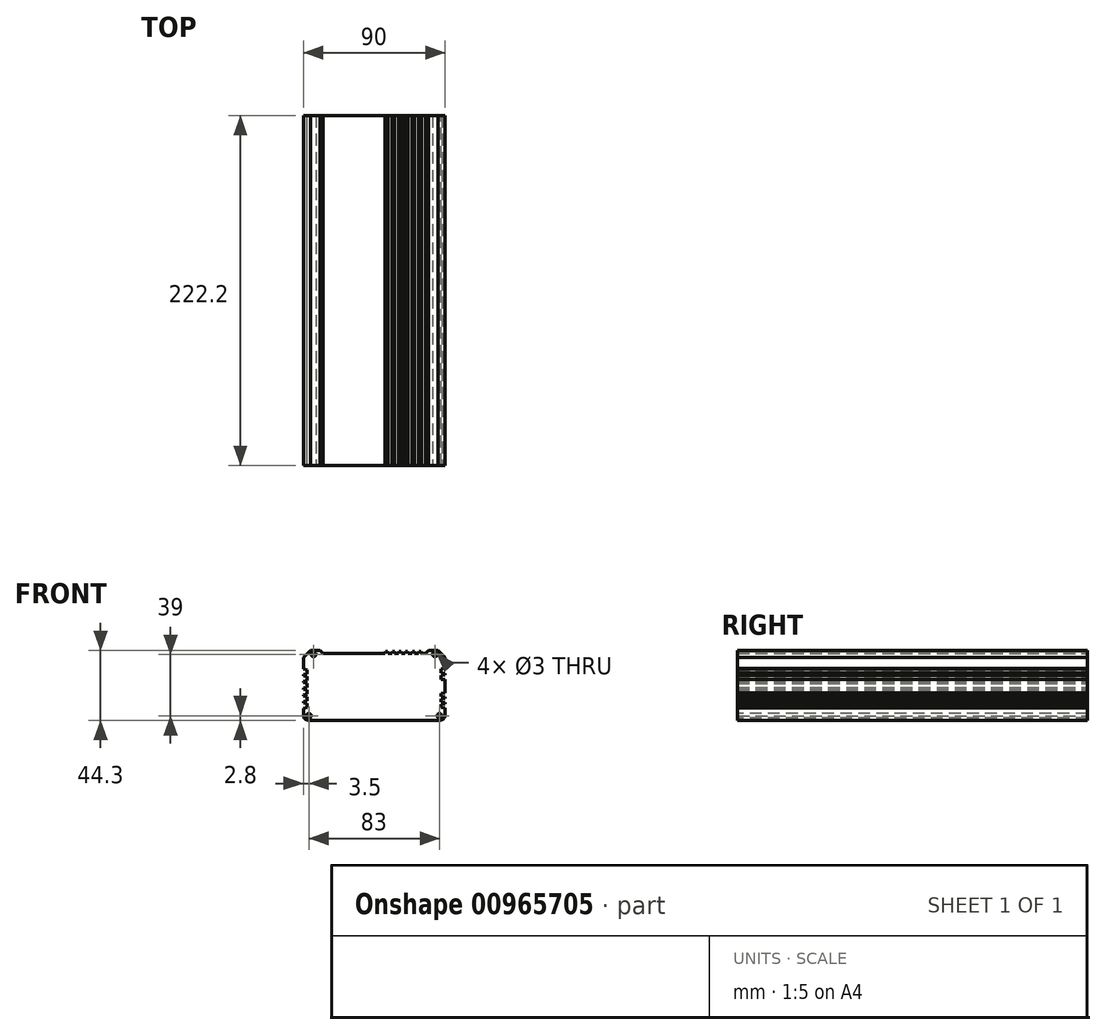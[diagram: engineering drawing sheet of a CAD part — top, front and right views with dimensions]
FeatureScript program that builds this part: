
annotation { "Feature Type Name" : "Feature", "Feature Type Description" : "" }
export const myFeature = defineFeature(function(context is Context, id is Id, definition is map)
    precondition{}
    {
        {
            var Q0;
            Q0=qCreatedBy(makeId("Front.planeOp"),FACE);
            var sketch = newSketch(context, id + "F0", { "sketchPlane" : qUnion([Q0])});
            skLineSegment(sketch, "E0", {"start": v(28.5, 43.8) * mm, "end": v(28.25, 42.3) * mm});
            skLineSegment(sketch, "E1", {"start": v(28.25, 42.3) * mm, "end": v(25.75, 42.3) * mm});
            skLineSegment(sketch, "E2", {"start": v(25.75, 42.3) * mm, "end": v(25.5, 43.8) * mm});
            skPoint(sketch, "E3", {"position": v(27, 42.3) * mm});
            skPoint(sketch, "E4", {"position": v(27, 43.3) * mm});
            skPoint(sketch, "E5.1.0.1", {"position": v(22.75, 42.3) * mm});
            skLineSegment(sketch, "E5.1.0.3", {"start": v(24.25, 43.8) * mm, "end": v(24, 42.3) * mm});
            skLineSegment(sketch, "E5.1.0.4", {"start": v(24, 42.3) * mm, "end": v(21.5, 42.3) * mm});
            skLineSegment(sketch, "E5.1.0.5", {"start": v(21.5, 42.3) * mm, "end": v(21.25, 43.8) * mm});
            skPoint(sketch, "E5.2.0.1", {"position": v(18.5, 42.3) * mm});
            skLineSegment(sketch, "E5.2.0.3", {"start": v(20, 43.8) * mm, "end": v(19.75, 42.3) * mm});
            skLineSegment(sketch, "E5.2.0.4", {"start": v(19.75, 42.3) * mm, "end": v(17.25, 42.3) * mm});
            skLineSegment(sketch, "E5.2.0.5", {"start": v(17.25, 42.3) * mm, "end": v(17, 43.8) * mm});
            skPoint(sketch, "E5.3.0.1", {"position": v(14.25, 42.3) * mm});
            skLineSegment(sketch, "E5.3.0.3", {"start": v(15.75, 43.8) * mm, "end": v(15.5, 42.3) * mm});
            skLineSegment(sketch, "E5.3.0.4", {"start": v(15.5, 42.3) * mm, "end": v(13, 42.3) * mm});
            skLineSegment(sketch, "E5.3.0.5", {"start": v(13, 42.3) * mm, "end": v(12.75, 43.8) * mm});
            skPoint(sketch, "E5.4.0.1", {"position": v(10, 42.3) * mm});
            skLineSegment(sketch, "E5.4.0.3", {"start": v(11.5, 43.8) * mm, "end": v(11.25, 42.3) * mm});
            skLineSegment(sketch, "E5.4.0.4", {"start": v(11.25, 42.3) * mm, "end": v(8.75, 42.3) * mm});
            skLineSegment(sketch, "E5.4.0.5", {"start": v(8.75, 42.3) * mm, "end": v(8.5, 43.8) * mm});
            skLineSegment(sketch, "E5.direction1", {"start": v(25.75, 42.3) * mm, "end": v(21.5, 42.3) * mm, "construction": true});
            skLineSegment(sketch, "E6", {"start": v(34.5, 44.3) * mm, "end": v(32.5, 42.3) * mm});
            skLineSegment(sketch, "E7", {"start": v(32.5, 42.3) * mm, "end": v(30, 42.3) * mm});
            skLineSegment(sketch, "E8", {"start": v(30, 42.3) * mm, "end": v(29.75, 43.8) * mm});
            skLineSegment(sketch, "E9", {"start": v(24.25, 43.8) * mm, "end": v(25.5, 43.8) * mm});
            skLineSegment(sketch, "E10", {"start": v(28.5, 43.8) * mm, "end": v(29.75, 43.8) * mm});
            skLineSegment(sketch, "E11", {"start": v(19.75, 42.3) * mm, "end": v(21.5, 42.3) * mm, "construction": true});
            skLineSegment(sketch, "E12", {"start": v(28.25, 42.3) * mm, "end": v(30, 42.3) * mm, "construction": true});
            skLineSegment(sketch, "E13", {"start": v(45, 39.8) * mm, "end": v(40.5, 44.3) * mm});
            skLineSegment(sketch, "E14.MirrorCS", {"start": v(-45, 39.8) * mm, "end": v(-40.5, 44.3) * mm});
            skLineSegment(sketch, "E15.MirrorCS", {"start": v(-34.5, 44.3) * mm, "end": v(-32.5, 42.3) * mm});
            skLineSegment(sketch, "E16", {"start": v(-32.5, 42.3) * mm, "end": v(7, 42.3) * mm});
            skLineSegment(sketch, "E17", {"start": v(7, 42.3) * mm, "end": v(7.25, 43.8) * mm});
            skLineSegment(sketch, "E18", {"start": v(8.75, 42.3) * mm, "end": v(7, 42.3) * mm, "construction": true});
            skLineSegment(sketch, "E19", {"start": v(8.5, 43.8) * mm, "end": v(7.25, 43.8) * mm});
            skLineSegment(sketch, "E20", {"start": v(42.5, 17) * mm, "end": v(42.5, 15) * mm});
            skLineSegment(sketch, "E21", {"start": v(42.5, 15) * mm, "end": v(45, 14.75) * mm});
            skLineSegment(sketch, "E22", {"start": v(45, 17.25) * mm, "end": v(42.5, 17) * mm});
            skPoint(sketch, "E23", {"position": v(42.5, 16) * mm});
            skPoint(sketch, "E24.1.0.0", {"position": v(42.5, 12.5) * mm});
            skLineSegment(sketch, "E24.1.0.2", {"start": v(45, 13.75) * mm, "end": v(42.5, 13.5) * mm});
            skLineSegment(sketch, "E24.1.0.3", {"start": v(42.5, 11.5) * mm, "end": v(45, 11.25) * mm});
            skLineSegment(sketch, "E24.1.0.5", {"start": v(42.5, 13.5) * mm, "end": v(42.5, 11.5) * mm});
            skPoint(sketch, "E24.2.0.0", {"position": v(42.5, 9) * mm});
            skLineSegment(sketch, "E24.2.0.2", {"start": v(45, 10.25) * mm, "end": v(42.5, 10) * mm});
            skLineSegment(sketch, "E24.2.0.3", {"start": v(42.5, 8) * mm, "end": v(45, 7.75) * mm});
            skLineSegment(sketch, "E24.2.0.5", {"start": v(42.5, 10) * mm, "end": v(42.5, 8) * mm});
            skLineSegment(sketch, "E24.direction1", {"start": v(42.5, 15) * mm, "end": v(42.5, 11.5) * mm, "construction": true});
            skLineSegment(sketch, "E25", {"start": v(45, 32.75) * mm, "end": v(42.5, 32.5) * mm});
            skLineSegment(sketch, "E26", {"start": v(42.5, 32.5) * mm, "end": v(42.5, 30) * mm});
            skLineSegment(sketch, "E27", {"start": v(42.5, 30) * mm, "end": v(45, 29.75) * mm});
            skPoint(sketch, "E28", {"position": v(42.5, 31.25) * mm});
            skPoint(sketch, "E29.1.0.0", {"position": v(42.5, 27.25) * mm});
            skLineSegment(sketch, "E29.1.0.1", {"start": v(45, 28.75) * mm, "end": v(42.5, 28.5) * mm});
            skLineSegment(sketch, "E29.1.0.2", {"start": v(42.5, 28.5) * mm, "end": v(42.5, 26) * mm});
            skLineSegment(sketch, "E29.1.0.4", {"start": v(42.5, 26) * mm, "end": v(45, 25.75) * mm});
            skLineSegment(sketch, "E29.direction1", {"start": v(42.5, 30) * mm, "end": v(42.5, 26) * mm, "construction": true});
            skLineSegment(sketch, "E30.MirrorCS", {"start": v(-42.5, 29.5) * mm, "end": v(-45, 29) * mm});
            skLineSegment(sketch, "E31.MirrorCS", {"start": v(-45, 32.5) * mm, "end": v(-42.5, 32) * mm});
            skLineSegment(sketch, "E32.MirrorCS", {"start": v(-42.5, 32) * mm, "end": v(-42.5, 29.5) * mm});
            skLineSegment(sketch, "E33", {"start": v(-45, 39.8) * mm, "end": v(-45, 32.5) * mm});
            skLineSegment(sketch, "E34", {"start": v(40.5, 44.3) * mm, "end": v(34.5, 44.3) * mm});
            skLineSegment(sketch, "E35", {"start": v(11.5, 43.8) * mm, "end": v(12.75, 43.8) * mm});
            skLineSegment(sketch, "E36", {"start": v(15.75, 43.8) * mm, "end": v(17, 43.8) * mm});
            skLineSegment(sketch, "E37", {"start": v(20, 43.8) * mm, "end": v(21.25, 43.8) * mm});
            skLineSegment(sketch, "E38", {"start": v(45, 39.8) * mm, "end": v(45, 32.75) * mm});
            skLineSegment(sketch, "E39", {"start": v(45, 29.75) * mm, "end": v(45, 28.75) * mm});
            skLineSegment(sketch, "E40", {"start": v(45, 25.75) * mm, "end": v(45, 17.25) * mm});
            skLineSegment(sketch, "E41", {"start": v(45, 14.75) * mm, "end": v(45, 13.75) * mm});
            skLineSegment(sketch, "E42", {"start": v(45, 11.25) * mm, "end": v(45, 10.25) * mm});
            skLineSegment(sketch, "E43", {"start": v(-45, 29) * mm, "end": v(-45, 28.2) * mm});
            skLineSegment(sketch, "E44", {"start": v(-42.01, 0) * mm, "end": v(42, 0) * mm});
            skLineSegment(sketch, "E45", {"start": v(45, 3) * mm, "end": v(45, 7.75) * mm});
            skArc(sketch, "E46.filletArc", {"start": v(-45, 2.75) * mm, "mid": v(-44.04, 0.8) * mm, "end": v(-42.01, 0) * mm});
            skArc(sketch, "E47.filletArc", {"start": v(42, 0) * mm, "mid": v(44.12, 0.88) * mm, "end": v(45, 3) * mm});
            skLineSegment(sketch, "E48", {"start": v(-40.5, 44.3) * mm, "end": v(-34.5, 44.3) * mm});
            skPoint(sketch, "E49.positionSnap0", {"position": v(-42.5, 30.75) * mm});
            skLineSegment(sketch, "E50", {"start": v(-45, 32.5) * mm, "end": v(-45, 29) * mm, "construction": true});
            skPoint(sketch, "E51", {"position": v(-45, 30.75) * mm});
            skPoint(sketch, "E52.1.0.0", {"position": v(-45, 26.45) * mm});
            skLineSegment(sketch, "E52.1.0.1", {"start": v(-45, 28.2) * mm, "end": v(-42.5, 27.7) * mm});
            skLineSegment(sketch, "E52.1.0.2", {"start": v(-42.5, 25.2) * mm, "end": v(-45, 24.7) * mm});
            skPoint(sketch, "E52.1.0.3", {"position": v(-42.5, 26.45) * mm});
            skLineSegment(sketch, "E52.1.0.4", {"start": v(-42.5, 27.7) * mm, "end": v(-42.5, 25.2) * mm});
            skLineSegment(sketch, "E52.1.0.5", {"start": v(-45, 24.7) * mm, "end": v(-45, 23.9) * mm});
            skLineSegment(sketch, "E52.1.0.6", {"start": v(-45, 28.2) * mm, "end": v(-45, 24.7) * mm, "construction": true});
            skPoint(sketch, "E52.2.0.0", {"position": v(-45, 22.15) * mm});
            skLineSegment(sketch, "E52.2.0.1", {"start": v(-45, 23.9) * mm, "end": v(-42.5, 23.4) * mm});
            skLineSegment(sketch, "E52.2.0.2", {"start": v(-42.5, 20.9) * mm, "end": v(-45, 20.4) * mm});
            skPoint(sketch, "E52.2.0.3", {"position": v(-42.5, 22.15) * mm});
            skLineSegment(sketch, "E52.2.0.4", {"start": v(-42.5, 23.4) * mm, "end": v(-42.5, 20.9) * mm});
            skLineSegment(sketch, "E52.2.0.5", {"start": v(-45, 20.4) * mm, "end": v(-45, 19.6) * mm});
            skLineSegment(sketch, "E52.2.0.6", {"start": v(-45, 23.9) * mm, "end": v(-45, 20.4) * mm, "construction": true});
            skPoint(sketch, "E52.3.0.0", {"position": v(-45, 17.85) * mm});
            skLineSegment(sketch, "E52.3.0.1", {"start": v(-45, 19.6) * mm, "end": v(-42.5, 19.1) * mm});
            skLineSegment(sketch, "E52.3.0.2", {"start": v(-42.5, 16.6) * mm, "end": v(-45, 16.1) * mm});
            skPoint(sketch, "E52.3.0.3", {"position": v(-42.5, 17.85) * mm});
            skLineSegment(sketch, "E52.3.0.4", {"start": v(-42.5, 19.1) * mm, "end": v(-42.5, 16.6) * mm});
            skLineSegment(sketch, "E52.3.0.5", {"start": v(-45, 16.1) * mm, "end": v(-45, 15.3) * mm});
            skLineSegment(sketch, "E52.3.0.6", {"start": v(-45, 19.6) * mm, "end": v(-45, 16.1) * mm, "construction": true});
            skPoint(sketch, "E52.4.0.0", {"position": v(-45, 13.55) * mm});
            skLineSegment(sketch, "E52.4.0.1", {"start": v(-45, 15.3) * mm, "end": v(-42.5, 14.8) * mm});
            skLineSegment(sketch, "E52.4.0.2", {"start": v(-42.5, 12.3) * mm, "end": v(-45, 11.8) * mm});
            skPoint(sketch, "E52.4.0.3", {"position": v(-42.5, 13.55) * mm});
            skLineSegment(sketch, "E52.4.0.4", {"start": v(-42.5, 14.8) * mm, "end": v(-42.5, 12.3) * mm});
            skLineSegment(sketch, "E52.4.0.5", {"start": v(-45, 11.8) * mm, "end": v(-45, 11) * mm});
            skLineSegment(sketch, "E52.4.0.6", {"start": v(-45, 15.3) * mm, "end": v(-45, 11.8) * mm, "construction": true});
            skPoint(sketch, "E52.5.0.0", {"position": v(-45, 9.25) * mm});
            skLineSegment(sketch, "E52.5.0.1", {"start": v(-45, 11) * mm, "end": v(-42.5, 10.5) * mm});
            skLineSegment(sketch, "E52.5.0.2", {"start": v(-42.5, 8) * mm, "end": v(-45, 7.5) * mm});
            skPoint(sketch, "E52.5.0.3", {"position": v(-42.5, 9.25) * mm});
            skLineSegment(sketch, "E52.5.0.4", {"start": v(-42.5, 10.5) * mm, "end": v(-42.5, 8) * mm});
            skLineSegment(sketch, "E52.5.0.6", {"start": v(-45, 11) * mm, "end": v(-45, 7.5) * mm, "construction": true});
            skLineSegment(sketch, "E52.direction1", {"start": v(-45, 28.2) * mm, "end": v(-45, 23.9) * mm, "construction": true});
            skLineSegment(sketch, "E53", {"start": v(-45, 7.5) * mm, "end": v(-45, 2.75) * mm});
            skLineSegment(sketch, "E54", {"start": v(45, 32.75) * mm, "end": v(45, 29.75) * mm, "construction": true});
            skPoint(sketch, "E55", {"position": v(45, 31.25) * mm});
            skLineSegment(sketch, "E56", {"start": v(45, 17.25) * mm, "end": v(45, 14.75) * mm, "construction": true});
            skPoint(sketch, "E57", {"position": v(45, 16) * mm});
            skLineSegment(sketch, "E58", {"start": v(45, 17.25) * mm, "end": v(42.5, 15) * mm, "construction": true});
            skLineSegment(sketch, "E59", {"start": v(45, 14.75) * mm, "end": v(42.5, 17) * mm, "construction": true});
            skLineSegment(sketch, "E60", {"start": v(45, 13.75) * mm, "end": v(42.5, 11.5) * mm, "construction": true});
            skLineSegment(sketch, "E61", {"start": v(45, 11.25) * mm, "end": v(42.5, 13.5) * mm, "construction": true});
            skLineSegment(sketch, "E62", {"start": v(42.5, 10) * mm, "end": v(45, 7.75) * mm, "construction": true});
            skLineSegment(sketch, "E63", {"start": v(42.5, 8) * mm, "end": v(45, 10.25) * mm, "construction": true});
            skSolve(sketch);
        }
        {
            var Q0;
            Q0=qSketchRegion(id+"F0",true);
            extrude(context, id + "F1", {"entities" : qUnion([Q0]), "endBound" : BoundingType.SYMMETRIC, "depth" : 222.2 * mm, "offsetDistance" : 25 * mm});
        }
        {
            var Q0;
            Q0=makeQuery(id+"F1.opExtrude","CAP_FACE",FACE,{"disambiguationData":[OSD([sQuery(id+"F0.wireOp",EDGE,"E0"),sQuery(id+"F0.wireOp",EDGE,"E1"),sQuery(id+"F0.wireOp",EDGE,"E2"),sQuery(id+"F0.wireOp",EDGE,"E5.1.0.3"),sQuery(id+"F0.wireOp",EDGE,"E5.1.0.4"),sQuery(id+"F0.wireOp",EDGE,"E5.1.0.5"),sQuery(id+"F0.wireOp",EDGE,"E5.2.0.3"),sQuery(id+"F0.wireOp",EDGE,"E5.2.0.4"),sQuery(id+"F0.wireOp",EDGE,"E5.2.0.5"),sQuery(id+"F0.wireOp",EDGE,"E5.3.0.3"),sQuery(id+"F0.wireOp",EDGE,"E5.3.0.4"),sQuery(id+"F0.wireOp",EDGE,"E5.3.0.5"),sQuery(id+"F0.wireOp",EDGE,"E5.4.0.3"),sQuery(id+"F0.wireOp",EDGE,"E5.4.0.4"),sQuery(id+"F0.wireOp",EDGE,"E5.4.0.5"),sQuery(id+"F0.wireOp",EDGE,"E6"),sQuery(id+"F0.wireOp",EDGE,"E7"),sQuery(id+"F0.wireOp",EDGE,"E8"),sQuery(id+"F0.wireOp",EDGE,"E9"),sQuery(id+"F0.wireOp",EDGE,"E10"),sQuery(id+"F0.wireOp",EDGE,"E13"),sQuery(id+"F0.wireOp",EDGE,"E14.MirrorCS"),sQuery(id+"F0.wireOp",EDGE,"E15.MirrorCS"),sQuery(id+"F0.wireOp",EDGE,"E16"),sQuery(id+"F0.wireOp",EDGE,"E17"),sQuery(id+"F0.wireOp",EDGE,"E19"),sQuery(id+"F0.wireOp",EDGE,"E20"),sQuery(id+"F0.wireOp",EDGE,"E21"),sQuery(id+"F0.wireOp",EDGE,"E22"),sQuery(id+"F0.wireOp",EDGE,"E24.1.0.2"),sQuery(id+"F0.wireOp",EDGE,"E24.1.0.3"),sQuery(id+"F0.wireOp",EDGE,"E24.1.0.5"),sQuery(id+"F0.wireOp",EDGE,"E24.2.0.2"),sQuery(id+"F0.wireOp",EDGE,"E24.2.0.3"),sQuery(id+"F0.wireOp",EDGE,"E24.2.0.5"),sQuery(id+"F0.wireOp",EDGE,"E25"),sQuery(id+"F0.wireOp",EDGE,"E26"),sQuery(id+"F0.wireOp",EDGE,"E27"),sQuery(id+"F0.wireOp",EDGE,"E29.1.0.1"),sQuery(id+"F0.wireOp",EDGE,"E29.1.0.2"),sQuery(id+"F0.wireOp",EDGE,"E29.1.0.4"),sQuery(id+"F0.wireOp",EDGE,"E30.MirrorCS"),sQuery(id+"F0.wireOp",EDGE,"E31.MirrorCS"),sQuery(id+"F0.wireOp",EDGE,"E32.MirrorCS"),sQuery(id+"F0.wireOp",EDGE,"E33"),sQuery(id+"F0.wireOp",EDGE,"E34"),sQuery(id+"F0.wireOp",EDGE,"E35"),sQuery(id+"F0.wireOp",EDGE,"E36"),sQuery(id+"F0.wireOp",EDGE,"E37"),sQuery(id+"F0.wireOp",EDGE,"E38"),sQuery(id+"F0.wireOp",EDGE,"E39"),sQuery(id+"F0.wireOp",EDGE,"E40"),sQuery(id+"F0.wireOp",EDGE,"E41"),sQuery(id+"F0.wireOp",EDGE,"E42"),sQuery(id+"F0.wireOp",EDGE,"E43"),sQuery(id+"F0.wireOp",EDGE,"E44"),sQuery(id+"F0.wireOp",EDGE,"E45"),sQuery(id+"F0.wireOp",EDGE,"E46.filletArc"),sQuery(id+"F0.wireOp",EDGE,"E47.filletArc"),sQuery(id+"F0.wireOp",EDGE,"E48"),sQuery(id+"F0.wireOp",EDGE,"E52.1.0.1"),sQuery(id+"F0.wireOp",EDGE,"E52.1.0.2"),sQuery(id+"F0.wireOp",EDGE,"E52.1.0.4"),sQuery(id+"F0.wireOp",EDGE,"E52.1.0.5"),sQuery(id+"F0.wireOp",EDGE,"E52.2.0.1"),sQuery(id+"F0.wireOp",EDGE,"E52.2.0.2"),sQuery(id+"F0.wireOp",EDGE,"E52.2.0.4"),sQuery(id+"F0.wireOp",EDGE,"E52.2.0.5"),sQuery(id+"F0.wireOp",EDGE,"E52.3.0.1"),sQuery(id+"F0.wireOp",EDGE,"E52.3.0.2"),sQuery(id+"F0.wireOp",EDGE,"E52.3.0.4"),sQuery(id+"F0.wireOp",EDGE,"E52.3.0.5"),sQuery(id+"F0.wireOp",EDGE,"E52.4.0.1"),sQuery(id+"F0.wireOp",EDGE,"E52.4.0.2"),sQuery(id+"F0.wireOp",EDGE,"E52.4.0.4"),sQuery(id+"F0.wireOp",EDGE,"E52.4.0.5"),sQuery(id+"F0.wireOp",EDGE,"E52.5.0.1"),sQuery(id+"F0.wireOp",EDGE,"E52.5.0.2"),sQuery(id+"F0.wireOp",EDGE,"E52.5.0.4"),sQuery(id+"F0.wireOp",EDGE,"E53")])],"isStart":false});
            var sketch = newSketch(context, id + "F2", { "sketchPlane" : qUnion([Q0])});
            skCircle(sketch, "E64", {"center": v(-38.5, 41.8) * mm, "radius": 1.5 * mm});
            skCircle(sketch, "E65", {"center": v(38.5, 41.8) * mm, "radius": 1.5 * mm});
            skCircle(sketch, "E66", {"center": v(41.5, 2.8) * mm, "radius": 1.5 * mm});
            skCircle(sketch, "E67", {"center": v(-41.5, 2.8) * mm, "radius": 1.5 * mm});
            skLineSegment(sketch, "E68", {"start": v(-38.5, 41.8) * mm, "end": v(38.5, 41.8) * mm, "construction": true});
            skPoint(sketch, "E69", {"position": v(0, 41.8) * mm});
            skLineSegment(sketch, "E70", {"start": v(45, 39.8) * mm, "end": v(-45, 39.8) * mm, "construction": true});
            skPoint(sketch, "E71", {"position": v(0, 39.8) * mm});
            skLineSegment(sketch, "E72", {"start": v(-41.5, 2.8) * mm, "end": v(41.5, 2.8) * mm, "construction": true});
            skLineSegment(sketch, "E73", {"start": v(-45, 2.75) * mm, "end": v(45, 3) * mm, "construction": true});
            skPoint(sketch, "E74", {"position": v(0, 2.8) * mm});
            skPoint(sketch, "E75", {"position": v(0, 2.88) * mm});
            skSolve(sketch);
        }
        {
            var Q0;
            Q0=qSketchRegion(id+"F2",true);
            extrude(context, id + "F3", {"entities" : qUnion([Q0]), "operationType" : NewBodyOperationType.REMOVE, "endBound" : BoundingType.THROUGH_ALL, "oppositeDirection" : true, "depth" : 25 * mm, "offsetDistance" : 25 * mm});
        }
    });
